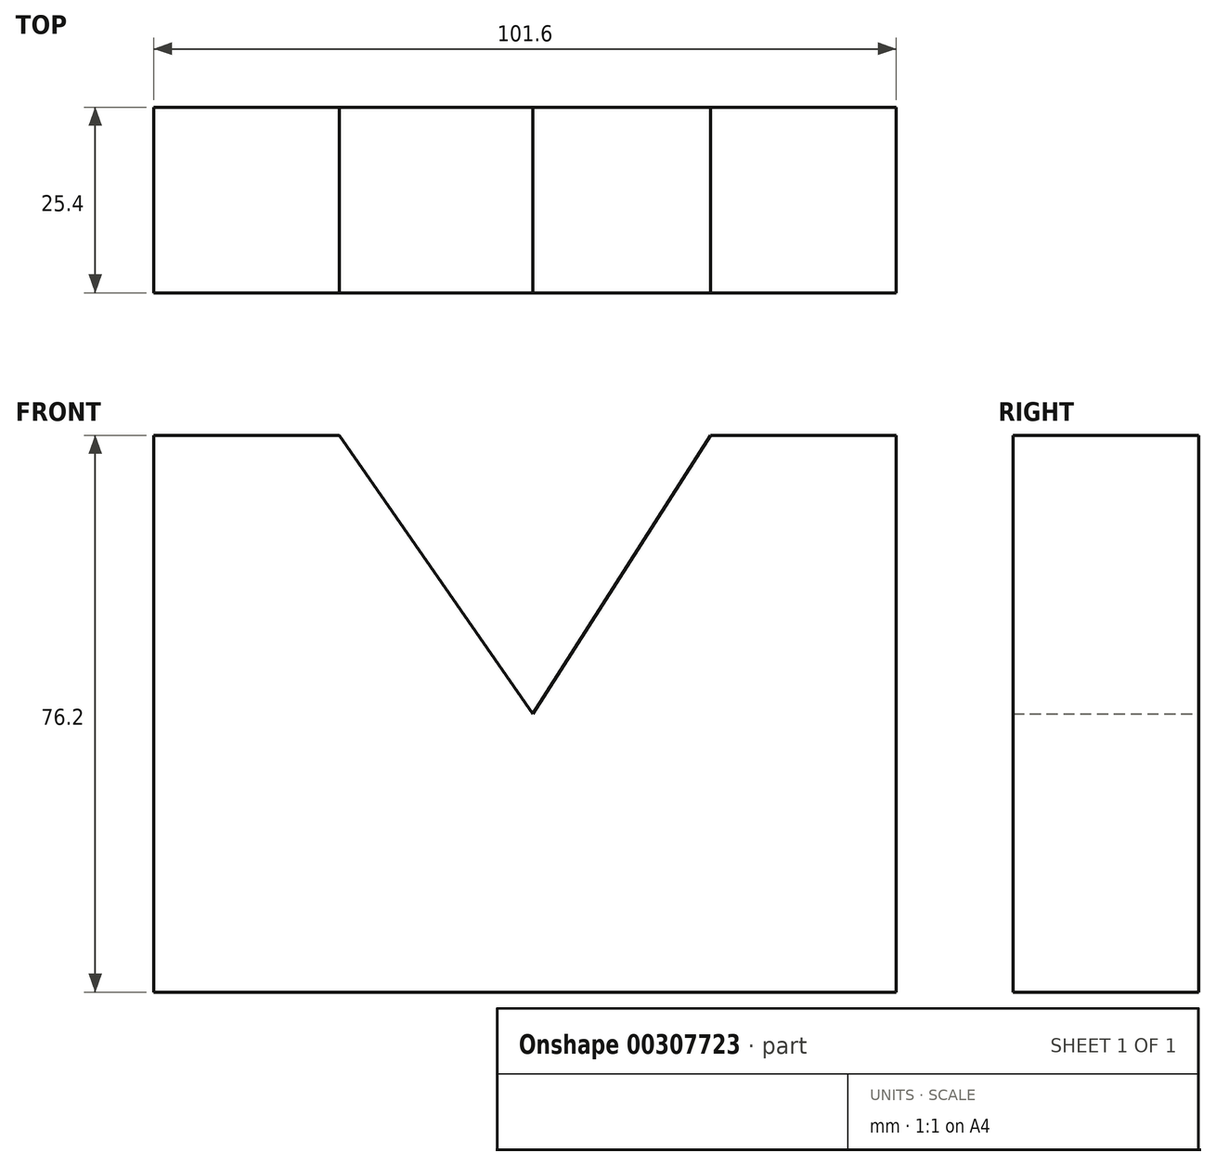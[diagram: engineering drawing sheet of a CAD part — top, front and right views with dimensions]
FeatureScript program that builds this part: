
annotation { "Feature Type Name" : "Feature", "Feature Type Description" : "" }
export const myFeature = defineFeature(function(context is Context, id is Id, definition is map)
    precondition{}
    {
        {
            var Q0;
            Q0=qCreatedBy(makeId("Front.planeOp"),FACE);
            var sketch = newSketch(context, id + "F0", { "sketchPlane" : qUnion([Q0])});
            skLineSegment(sketch, "E0", {"start": v(24.3, 46.83) * mm, "end": v(49.7, 46.83) * mm});
            skLineSegment(sketch, "E1", {"start": v(49.7, 46.83) * mm, "end": v(49.7, -29.37) * mm});
            skLineSegment(sketch, "E2", {"start": v(49.7, -29.37) * mm, "end": v(-51.9, -29.37) * mm});
            skLineSegment(sketch, "E3", {"start": v(-51.9, -29.37) * mm, "end": v(-51.9, 46.83) * mm});
            skLineSegment(sketch, "E4", {"start": v(-51.9, 46.83) * mm, "end": v(-26.5, 46.83) * mm});
            skLineSegment(sketch, "E5", {"start": v(-26.5, 46.83) * mm, "end": v(0, 8.73) * mm});
            skLineSegment(sketch, "E6", {"start": v(0, 8.73) * mm, "end": v(24.3, 46.83) * mm});
            skSolve(sketch);
        }
        {
            var Q0;
            Q0=makeQuery(id+"F0.imprint","IMPRINT",FACE,{"disambiguationData":[TD([[makeQuery(id+"F0.imprint","IMPRINT",EDGE,{"derivedFrom":sQuery(id+"F0.wireOp",EDGE,"E0")}),-1.0]])]});
            extrude(context, id + "F1", {"entities" : qUnion([Q0]), "depth" : 25.4 * mm});
        }
    });
